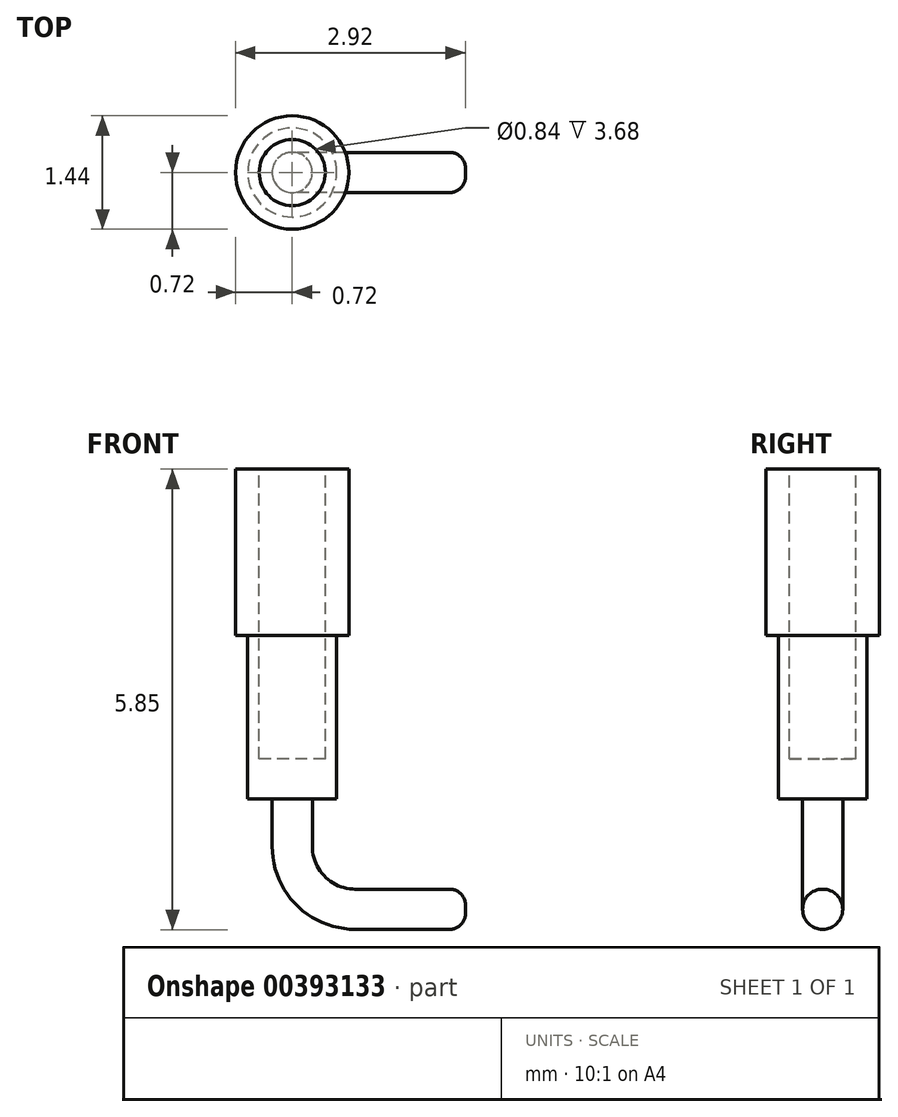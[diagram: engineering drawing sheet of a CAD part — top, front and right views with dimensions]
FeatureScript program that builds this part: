
annotation { "Feature Type Name" : "Feature", "Feature Type Description" : "" }
export const myFeature = defineFeature(function(context is Context, id is Id, definition is map)
    precondition{}
    {
        {
            var Q0;
            Q0=qCreatedBy(makeId("Top.planeOp"),FACE);
            var sketch = newSketch(context, id + "F0", { "sketchPlane" : qUnion([Q0])});
            skCircle(sketch, "E0", {"center": v(0, 0) * mm, "radius": 0.42 * mm});
            skCircle(sketch, "E1", {"center": v(0, 0) * mm, "radius": 0.72 * mm});
            skSolve(sketch);
        }
        {
            var Q0;
            Q0 = qSketchRegion(id + "F0", true);
            extrude(context, id + "F1", {"entities" : qUnion([Q0]), "oppositeDirection" : true, "depth" : 2.1 * mm});
        }
        {
            var Q0;
            Q0=makeQuery(id+"F1.opExtrude","CAP_FACE",FACE,{"disambiguationData":[OSD([sQuery(id+"F0.wireOp",EDGE,"E0"),sQuery(id+"F0.wireOp",EDGE,"E1")])],"isStart":false});
            var sketch = newSketch(context, id + "F2", { "sketchPlane" : qUnion([Q0])});
            skCircle(sketch, "E2.0", {"center": v(0, 0) * mm, "radius": 0.42 * mm});
            skCircle(sketch, "E3", {"center": v(0, 0) * mm, "radius": 0.56 * mm});
            skSolve(sketch);
        }
        {
            var Q0;
            Q0 = qSketchRegion(id + "F2", true);
            extrude(context, id + "F3", {"entities" : qUnion([Q0]), "operationType" : NewBodyOperationType.ADD, "depth" : 1.57 * mm});
        }
        {
            var Q0;
            Q0=makeQuery(id+"F3.opExtrude","CAP_FACE",FACE,{"disambiguationData":[OSD([sQuery(id+"F2.wireOp",EDGE,"E2.0"),sQuery(id+"F2.wireOp",EDGE,"E3")])],"isStart":false});
            var sketch = newSketch(context, id + "F4", { "sketchPlane" : qUnion([Q0])});
            skCircle(sketch, "E4.0", {"center": v(0, 0) * mm, "radius": 0.56 * mm});
            skSolve(sketch);
        }
        {
            var Q0;
            Q0=makeQuery(id+"F4.imprint","IMPRINT",FACE,{"disambiguationData":[TD([[makeQuery(id+"F4.imprint","IMPRINT",EDGE,{"derivedFrom":makeQuery(id+"F3.opExtrude","CAP_EDGE",EDGE,{"disambiguationData":[OSD([sQuery(id+"F2.wireOp",EDGE,"E2.0")])],"isStart":false})}),-1.0]])]});
            var Q1;
            Q1=makeQuery(id+"F4.imprint","IMPRINT",FACE,{"disambiguationData":[TD([[makeQuery(id+"F4.imprint","IMPRINT",EDGE,{"derivedFrom":sQuery(id+"F4.wireOp",EDGE,"E4.0")}),1.0]])]});
            extrude(context, id + "F5", {"entities" : qUnion([Q0, Q1]), "operationType" : NewBodyOperationType.ADD, "depth" : 0.51 * mm});
        }
        {
            var Q0;
            Q0=qCreatedBy(makeId("Front.planeOp"),FACE);
            var sketch = newSketch(context, id + "F6", { "sketchPlane" : qUnion([Q0])});
            skLineSegment(sketch, "E5.0", {"start": v(0.56, -4.2) * mm, "end": v(-0.56, -4.2) * mm, "construction": true});
            skLineSegment(sketch, "E6", {"start": v(0, -4.2) * mm, "end": v(0, -4.8) * mm});
            skLineSegment(sketch, "E7", {"start": v(0.8, -5.6) * mm, "end": v(2.2, -5.6) * mm});
            skPoint(sketch, "E8.visualSharp", {"position": v(0, -5.6) * mm});
            skArc(sketch, "E8.filletArc", {"start": v(0, -4.8) * mm, "mid": v(0.23, -5.36) * mm, "end": v(0.8, -5.6) * mm});
            skSolve(sketch);
        }
        {
            var Q0;
            Q0=makeQuery(id+"F5.opExtrude","CAP_FACE",FACE,{"disambiguationData":[OSD([sQuery(id+"F4.wireOp",EDGE,"E4.0")])],"isStart":false});
            var sketch = newSketch(context, id + "F7", { "sketchPlane" : qUnion([Q0])});
            skCircle(sketch, "E9", {"center": v(0, 0) * mm, "radius": 0.26 * mm});
            skSolve(sketch);
        }
        {
            var Q0;
            Q0=makeQuery(id+"F7.imprint","IMPRINT",FACE,{"disambiguationData":[TD([[makeQuery(id+"F7.imprint","IMPRINT",EDGE,{"derivedFrom":sQuery(id+"F7.wireOp",EDGE,"E9")}),1.0]])]});
            var Q1;
            Q1 = qConstructionFilter(qBodyType(qCreatedBy(id + "F6" ,EDGE), BodyType.WIRE), ConstructionObject.NO);
            sweep(context, id + "F8", {"operationType" : NewBodyOperationType.ADD, "profiles" : qUnion([Q0]), "path" : qUnion([Q1])});
        }
        {
            var Q0;
            Q0=makeQuery(id+"F8.opSweep","CAP_FACE",FACE,{"disambiguationData":[OSD([sQuery(id+"F6.wireOp",VERTEX,"E7.end"),sQuery(id+"F7.wireOp",EDGE,"E9")])],"isStart":false});
            fillet(context, id + "F9", {"entities" : qUnion([Q0]), "radius" : 0.2 * mm, "tangentPropagation" : true, "allowEdgeOverflow" : false});
        }
    });
